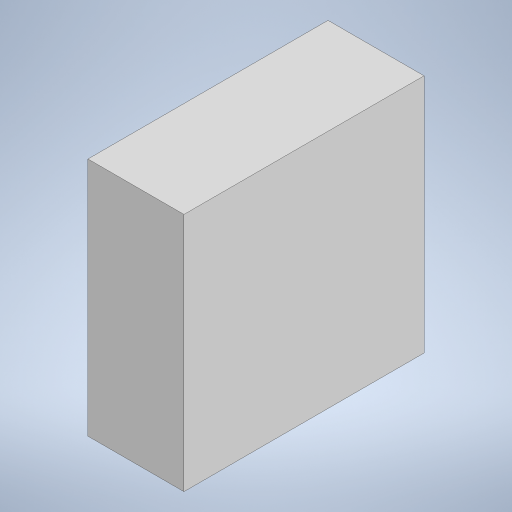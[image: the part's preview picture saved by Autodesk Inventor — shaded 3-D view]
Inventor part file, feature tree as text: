
AUTODESK INVENTOR PART (.ipt)
format: ipt  version: 2023 (Build 270158000, 158)  size: 173,056 bytes
history: native  units: mm
features: extrude x1, sketch x1
ambient origin geometry x8: Origin, YZ Plane, XZ Plane, XY Plane, X Axis, Y Axis, Z Axis, Center Point
bodies: Solid1 (feature_tree)
feature tree (2):
  extrude  "Extrusion1"  Depth=50.0mm
  sketch  "Sketch2"  dims[d0=20.0mm d1=50.0mm d2=50.0mm d3=0.0mm]
